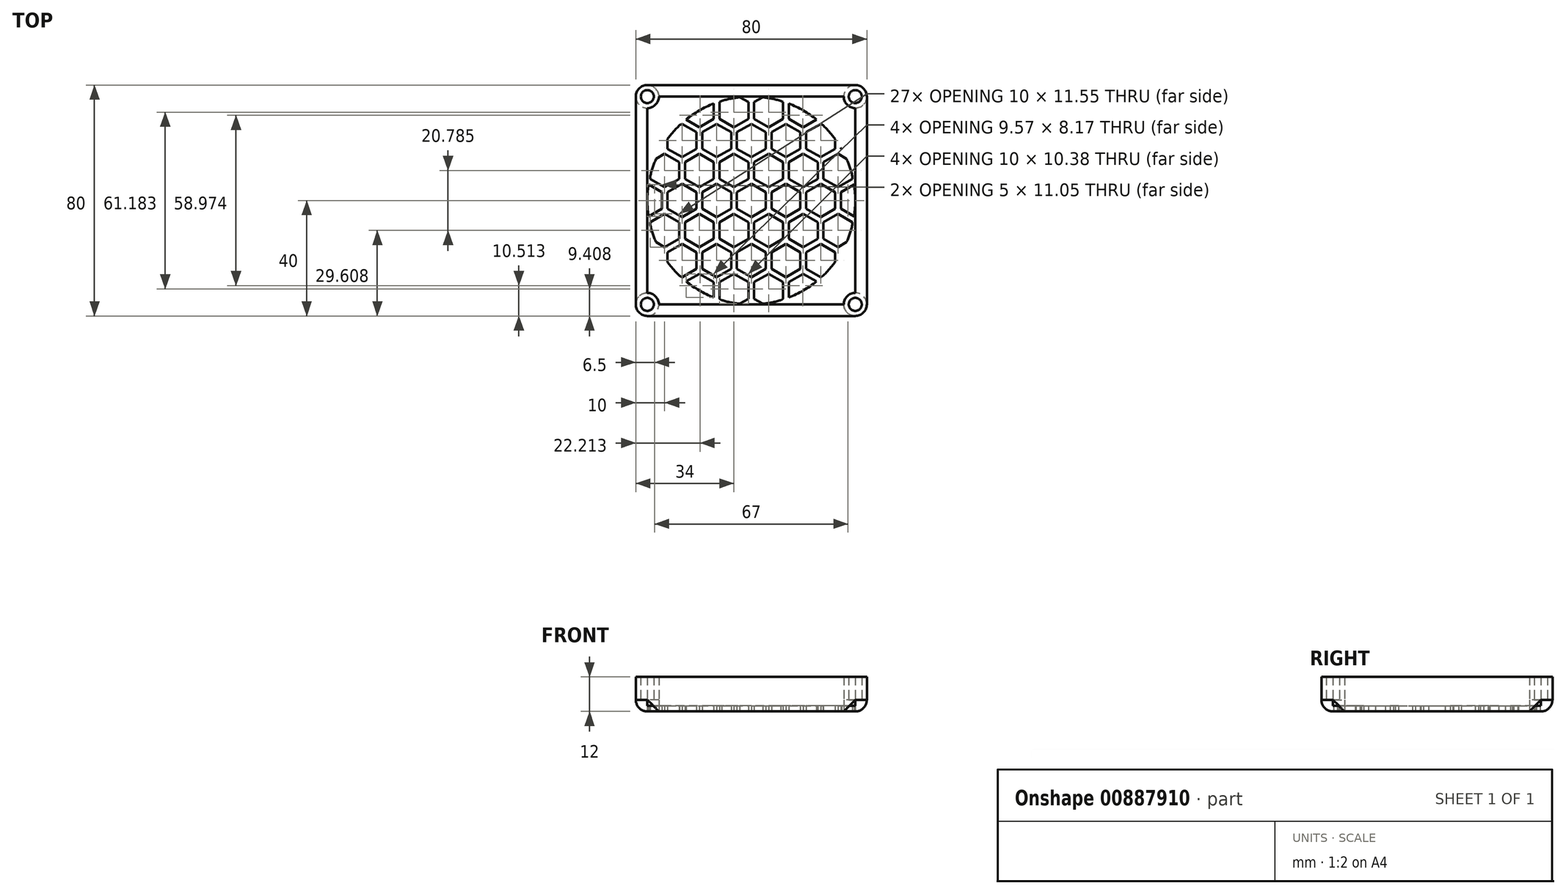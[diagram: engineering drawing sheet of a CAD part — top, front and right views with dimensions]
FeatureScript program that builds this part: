
annotation { "Feature Type Name" : "Feature", "Feature Type Description" : "" }
export const myFeature = defineFeature(function(context is Context, id is Id, definition is map)
    precondition{}
    {
        {
            var Q0;
            Q0=qCreatedBy(makeId("Top.planeOp"),FACE);
            var sketch = newSketch(context, id + "F0", { "sketchPlane" : qUnion([Q0])});
            skLineSegment(sketch, "E0.bottom", {"start": v(-36, 36) * mm, "end": v(36, 36) * mm});
            skLineSegment(sketch, "E0.top", {"start": v(-36, -36) * mm, "end": v(36, -36) * mm});
            skLineSegment(sketch, "E0.left", {"start": v(-36, 36) * mm, "end": v(-36, -36) * mm});
            skLineSegment(sketch, "E0.right", {"start": v(36, 36) * mm, "end": v(36, -36) * mm});
            skPoint(sketch, "E0.middle", {"position": v(0, 0) * mm});
            skCircle(sketch, "E1", {"center": v(-36, 36) * mm, "radius": 2.25 * mm});
            skCircle(sketch, "E2", {"center": v(36, 36) * mm, "radius": 2.25 * mm});
            skCircle(sketch, "E3", {"center": v(36, -36) * mm, "radius": 2.25 * mm});
            skCircle(sketch, "E4", {"center": v(-36, -36) * mm, "radius": 2.25 * mm});
            skLineSegment(sketch, "E5.bottom", {"start": v(-40, 40) * mm, "end": v(40, 40) * mm});
            skLineSegment(sketch, "E5.top", {"start": v(-40, -40) * mm, "end": v(40, -40) * mm});
            skLineSegment(sketch, "E5.left", {"start": v(-40, 40) * mm, "end": v(-40, -40) * mm});
            skLineSegment(sketch, "E5.right", {"start": v(40, 40) * mm, "end": v(40, -40) * mm});
            skCircle(sketch, "E6", {"center": v(0, 0) * mm, "radius": 36 * mm});
            skCircle(sketch, "E7.cCircle", {"center": v(0, 0) * mm, "radius": 5 * mm, "construction": true});
            skLineSegment(sketch, "E7.0", {"start": v(-5, -2.89) * mm, "end": v(-5, 2.89) * mm});
            skLineSegment(sketch, "E7.1", {"start": v(-5, 2.89) * mm, "end": v(0, 5.77) * mm});
            skLineSegment(sketch, "E7.2", {"start": v(0, 5.77) * mm, "end": v(5, 2.89) * mm});
            skLineSegment(sketch, "E7.3", {"start": v(5, 2.89) * mm, "end": v(5, -2.89) * mm});
            skLineSegment(sketch, "E7.4", {"start": v(5, -2.89) * mm, "end": v(0, -5.77) * mm});
            skLineSegment(sketch, "E7.5", {"start": v(0, -5.77) * mm, "end": v(-5, -2.89) * mm});
            skPoint(sketch, "E7.0.midPoint", {"position": v(-5, 0) * mm});
            skPoint(sketch, "E8.0.1.0", {"position": v(-5, 20.78) * mm});
            skLineSegment(sketch, "E8.0.1.1", {"start": v(5, 17.9) * mm, "end": v(0, 15.01) * mm});
            skPoint(sketch, "E8.0.1.3", {"position": v(0, 20.78) * mm});
            skLineSegment(sketch, "E8.0.1.4", {"start": v(0, 26.56) * mm, "end": v(5, 23.67) * mm});
            skLineSegment(sketch, "E8.0.1.5", {"start": v(0, 15.01) * mm, "end": v(-5, 17.9) * mm});
            skLineSegment(sketch, "E8.0.1.6", {"start": v(-5, 17.9) * mm, "end": v(-5, 23.67) * mm});
            skLineSegment(sketch, "E8.0.1.7", {"start": v(-5, 23.67) * mm, "end": v(0, 26.56) * mm});
            skLineSegment(sketch, "E8.0.1.8", {"start": v(5, 23.67) * mm, "end": v(5, 17.9) * mm});
            skPoint(sketch, "E8.0.1.9", {"position": v(0, 20.78) * mm});
            skPoint(sketch, "E8.0.1.10", {"position": v(0, 20.78) * mm});
            skPoint(sketch, "E8.0.1.11", {"position": v(0, 20.78) * mm});
            skPoint(sketch, "E8.1.0.0", {"position": v(7, 0) * mm});
            skLineSegment(sketch, "E8.1.0.1", {"start": v(17, -2.89) * mm, "end": v(12, -5.77) * mm});
            skCircle(sketch, "E8.1.0.2", {"center": v(12, 0) * mm, "radius": 5 * mm, "construction": true});
            skPoint(sketch, "E8.1.0.3", {"position": v(12, 0) * mm});
            skLineSegment(sketch, "E8.1.0.4", {"start": v(12, 5.77) * mm, "end": v(17, 2.89) * mm});
            skLineSegment(sketch, "E8.1.0.5", {"start": v(12, -5.77) * mm, "end": v(7, -2.89) * mm});
            skLineSegment(sketch, "E8.1.0.6", {"start": v(7, -2.89) * mm, "end": v(7, 2.89) * mm});
            skLineSegment(sketch, "E8.1.0.7", {"start": v(7, 2.89) * mm, "end": v(12, 5.77) * mm});
            skLineSegment(sketch, "E8.1.0.8", {"start": v(17, 2.89) * mm, "end": v(17, -2.89) * mm});
            skPoint(sketch, "E8.1.0.9", {"position": v(12, 0) * mm});
            skPoint(sketch, "E8.1.0.10", {"position": v(12, 0) * mm});
            skPoint(sketch, "E8.1.0.11", {"position": v(12, 0) * mm});
            skPoint(sketch, "E8.1.1.0", {"position": v(7, 20.78) * mm});
            skLineSegment(sketch, "E8.1.1.1", {"start": v(17, 17.9) * mm, "end": v(12, 15.01) * mm});
            skPoint(sketch, "E8.1.1.3", {"position": v(12, 20.78) * mm});
            skLineSegment(sketch, "E8.1.1.4", {"start": v(12, 26.56) * mm, "end": v(17, 23.67) * mm});
            skLineSegment(sketch, "E8.1.1.5", {"start": v(12, 15.01) * mm, "end": v(7, 17.9) * mm});
            skLineSegment(sketch, "E8.1.1.6", {"start": v(7, 17.9) * mm, "end": v(7, 23.67) * mm});
            skLineSegment(sketch, "E8.1.1.7", {"start": v(7, 23.67) * mm, "end": v(12, 26.56) * mm});
            skLineSegment(sketch, "E8.1.1.8", {"start": v(17, 23.67) * mm, "end": v(17, 17.9) * mm});
            skPoint(sketch, "E8.1.1.9", {"position": v(12, 20.78) * mm});
            skPoint(sketch, "E8.1.1.10", {"position": v(12, 20.78) * mm});
            skPoint(sketch, "E8.1.1.11", {"position": v(12, 20.78) * mm});
            skPoint(sketch, "E8.2.0.0", {"position": v(19, 0) * mm});
            skLineSegment(sketch, "E8.2.0.1", {"start": v(29, -2.89) * mm, "end": v(24, -5.77) * mm});
            skPoint(sketch, "E8.2.0.3", {"position": v(24, 0) * mm});
            skLineSegment(sketch, "E8.2.0.4", {"start": v(24, 5.77) * mm, "end": v(29, 2.89) * mm});
            skLineSegment(sketch, "E8.2.0.5", {"start": v(24, -5.77) * mm, "end": v(19, -2.89) * mm});
            skLineSegment(sketch, "E8.2.0.6", {"start": v(19, -2.89) * mm, "end": v(19, 2.89) * mm});
            skLineSegment(sketch, "E8.2.0.7", {"start": v(19, 2.89) * mm, "end": v(24, 5.77) * mm});
            skLineSegment(sketch, "E8.2.0.8", {"start": v(29, 2.89) * mm, "end": v(29, -2.89) * mm});
            skPoint(sketch, "E8.2.0.9", {"position": v(24, 0) * mm});
            skPoint(sketch, "E8.2.0.10", {"position": v(24, 0) * mm});
            skPoint(sketch, "E8.2.0.11", {"position": v(24, 0) * mm});
            skPoint(sketch, "E8.2.1.0", {"position": v(19, 20.78) * mm});
            skLineSegment(sketch, "E8.2.1.1", {"start": v(29, 17.9) * mm, "end": v(24, 15.01) * mm});
            skPoint(sketch, "E8.2.1.3", {"position": v(24, 20.78) * mm});
            skLineSegment(sketch, "E8.2.1.4", {"start": v(24, 26.56) * mm, "end": v(24.8, 26.1) * mm});
            skLineSegment(sketch, "E8.2.1.5", {"start": v(24, 15.01) * mm, "end": v(19, 17.9) * mm});
            skLineSegment(sketch, "E8.2.1.6", {"start": v(19, 17.9) * mm, "end": v(19, 23.67) * mm});
            skLineSegment(sketch, "E8.2.1.7", {"start": v(19, 23.67) * mm, "end": v(24, 26.56) * mm});
            skLineSegment(sketch, "E8.2.1.8", {"start": v(29, 21.33) * mm, "end": v(29, 17.9) * mm});
            skPoint(sketch, "E8.2.1.9", {"position": v(24, 20.78) * mm});
            skPoint(sketch, "E8.2.1.10", {"position": v(24, 20.78) * mm});
            skPoint(sketch, "E8.2.1.11", {"position": v(24, 20.78) * mm});
            skPoint(sketch, "E8.3.0.0", {"position": v(31, 0) * mm});
            skPoint(sketch, "E8.3.0.3", {"position": v(36, 0) * mm});
            skLineSegment(sketch, "E8.3.0.5", {"start": v(35.57, -5.53) * mm, "end": v(31, -2.89) * mm});
            skLineSegment(sketch, "E8.3.0.6", {"start": v(31, -2.89) * mm, "end": v(31, 2.89) * mm});
            skLineSegment(sketch, "E8.3.0.7", {"start": v(31, 2.89) * mm, "end": v(35.57, 5.53) * mm});
            skPoint(sketch, "E8.3.0.9", {"position": v(36, 0) * mm});
            skPoint(sketch, "E8.3.0.10", {"position": v(36, 0) * mm});
            skPoint(sketch, "E8.3.0.11", {"position": v(36, 0) * mm});
            skLineSegment(sketch, "E8.3.1.6", {"start": v(31, 17.9) * mm, "end": v(31, 18.3) * mm});
            skLineSegment(sketch, "E8.direction1", {"start": v(-5, 0) * mm, "end": v(7, 0) * mm, "construction": true});
            skLineSegment(sketch, "E8.direction2", {"start": v(-5, 0) * mm, "end": v(-5, 20.78) * mm, "construction": true});
            skCircle(sketch, "E9.cCircle", {"center": v(6, 10.4) * mm, "radius": 5 * mm, "construction": true});
            skLineSegment(sketch, "E9.0", {"start": v(6, 16.17) * mm, "end": v(11, 13.28) * mm});
            skLineSegment(sketch, "E9.1", {"start": v(11, 13.28) * mm, "end": v(11, 7.5) * mm});
            skLineSegment(sketch, "E9.2", {"start": v(11, 7.5) * mm, "end": v(6, 4.62) * mm});
            skLineSegment(sketch, "E9.3", {"start": v(6, 4.62) * mm, "end": v(1, 7.5) * mm});
            skLineSegment(sketch, "E9.4", {"start": v(1, 7.5) * mm, "end": v(1, 13.28) * mm});
            skLineSegment(sketch, "E9.5", {"start": v(1, 13.28) * mm, "end": v(6, 16.17) * mm});
            skLineSegment(sketch, "E10", {"start": v(7, 20.78) * mm, "end": v(5, 20.78) * mm, "construction": true});
            skPoint(sketch, "E11", {"position": v(6, 20.78) * mm});
            skPoint(sketch, "E12", {"position": v(1, 10.4) * mm});
            skLineSegment(sketch, "E13.0.1.0", {"start": v(1, 28.3) * mm, "end": v(1, 34.06) * mm});
            skLineSegment(sketch, "E13.0.1.1", {"start": v(11, 28.3) * mm, "end": v(6, 25.4) * mm});
            skLineSegment(sketch, "E13.0.1.2", {"start": v(6, 25.4) * mm, "end": v(1, 28.3) * mm});
            skLineSegment(sketch, "E13.0.1.4", {"start": v(11, 34.06) * mm, "end": v(11, 28.3) * mm});
            skLineSegment(sketch, "E13.0.1.6", {"start": v(1, 34.06) * mm, "end": v(3.97, 35.78) * mm});
            skPoint(sketch, "E13.0.1.7", {"position": v(1, 31.18) * mm});
            skLineSegment(sketch, "E13.1.0.0", {"start": v(13, 7.5) * mm, "end": v(13, 13.28) * mm});
            skLineSegment(sketch, "E13.1.0.1", {"start": v(23, 7.5) * mm, "end": v(18, 4.62) * mm});
            skLineSegment(sketch, "E13.1.0.2", {"start": v(18, 4.62) * mm, "end": v(13, 7.5) * mm});
            skLineSegment(sketch, "E13.1.0.4", {"start": v(23, 13.28) * mm, "end": v(23, 7.5) * mm});
            skLineSegment(sketch, "E13.1.0.5", {"start": v(18, 16.17) * mm, "end": v(23, 13.28) * mm});
            skLineSegment(sketch, "E13.1.0.6", {"start": v(13, 13.28) * mm, "end": v(18, 16.17) * mm});
            skPoint(sketch, "E13.1.0.7", {"position": v(13, 10.4) * mm});
            skLineSegment(sketch, "E13.1.1.0", {"start": v(13, 28.3) * mm, "end": v(13, 33.57) * mm});
            skLineSegment(sketch, "E13.1.1.1", {"start": v(22.57, 28.04) * mm, "end": v(18, 25.4) * mm});
            skLineSegment(sketch, "E13.1.1.2", {"start": v(18, 25.4) * mm, "end": v(13, 28.3) * mm});
            skPoint(sketch, "E13.1.1.7", {"position": v(13, 31.18) * mm});
            skLineSegment(sketch, "E13.2.0.0", {"start": v(25, 7.5) * mm, "end": v(25, 13.28) * mm});
            skLineSegment(sketch, "E13.2.0.1", {"start": v(35, 7.5) * mm, "end": v(30, 4.62) * mm});
            skLineSegment(sketch, "E13.2.0.2", {"start": v(30, 4.62) * mm, "end": v(25, 7.5) * mm});
            skLineSegment(sketch, "E13.2.0.4", {"start": v(35, 8.43) * mm, "end": v(35, 7.5) * mm});
            skLineSegment(sketch, "E13.2.0.5", {"start": v(30, 16.17) * mm, "end": v(32.97, 14.45) * mm});
            skLineSegment(sketch, "E13.2.0.6", {"start": v(25, 13.28) * mm, "end": v(30, 16.17) * mm});
            skPoint(sketch, "E13.2.0.7", {"position": v(25, 10.4) * mm});
            skLineSegment(sketch, "E13.direction1", {"start": v(1, 10.4) * mm, "end": v(13, 10.4) * mm, "construction": true});
            skLineSegment(sketch, "E13.direction2", {"start": v(1, 10.4) * mm, "end": v(1, 31.18) * mm, "construction": true});
            skLineSegment(sketch, "E14.trimOffspring", {"start": v(10.2, 34.52) * mm, "end": v(11, 34.06) * mm});
            skLineSegment(sketch, "E15.trimOffspring", {"start": v(31.35, 17.7) * mm, "end": v(31, 17.9) * mm});
            skLineSegment(sketch, "E16.MirrorCS", {"start": v(-6, 25.4) * mm, "end": v(-1, 28.3) * mm});
            skLineSegment(sketch, "E17.MirrorCS", {"start": v(-1, 28.3) * mm, "end": v(-1, 34.06) * mm});
            skLineSegment(sketch, "E18.MirrorCS", {"start": v(-1, 34.06) * mm, "end": v(-3.97, 35.78) * mm});
            skLineSegment(sketch, "E19.MirrorCS", {"start": v(-11, 34.06) * mm, "end": v(-11, 28.3) * mm});
            skLineSegment(sketch, "E20.MirrorCS", {"start": v(-10.2, 34.52) * mm, "end": v(-11, 34.06) * mm});
            skLineSegment(sketch, "E21.MirrorCS", {"start": v(-11, 28.3) * mm, "end": v(-6, 25.4) * mm});
            skLineSegment(sketch, "E22.MirrorCS", {"start": v(-18, 25.4) * mm, "end": v(-13, 28.3) * mm});
            skLineSegment(sketch, "E23.MirrorCS", {"start": v(-13, 28.3) * mm, "end": v(-13, 33.57) * mm});
            skLineSegment(sketch, "E24.MirrorCS", {"start": v(-22.57, 28.04) * mm, "end": v(-18, 25.4) * mm});
            skLineSegment(sketch, "E25.MirrorCS", {"start": v(-7, 23.67) * mm, "end": v(-12, 26.56) * mm});
            skLineSegment(sketch, "E26.MirrorCS", {"start": v(-12, 26.56) * mm, "end": v(-17, 23.67) * mm});
            skLineSegment(sketch, "E27.MirrorCS", {"start": v(-17, 23.67) * mm, "end": v(-17, 17.9) * mm});
            skLineSegment(sketch, "E28.MirrorCS", {"start": v(-17, 17.9) * mm, "end": v(-12, 15.01) * mm});
            skLineSegment(sketch, "E29.MirrorCS", {"start": v(-12, 15.01) * mm, "end": v(-7, 17.9) * mm});
            skLineSegment(sketch, "E30.MirrorCS", {"start": v(-7, 17.9) * mm, "end": v(-7, 23.67) * mm});
            skLineSegment(sketch, "E31.MirrorCS", {"start": v(-1, 13.28) * mm, "end": v(-6, 16.17) * mm});
            skLineSegment(sketch, "E32.MirrorCS", {"start": v(-6, 16.17) * mm, "end": v(-11, 13.28) * mm});
            skLineSegment(sketch, "E33.MirrorCS", {"start": v(-11, 13.28) * mm, "end": v(-11, 7.5) * mm});
            skLineSegment(sketch, "E34.MirrorCS", {"start": v(-11, 7.5) * mm, "end": v(-6, 4.62) * mm});
            skLineSegment(sketch, "E35.MirrorCS", {"start": v(-6, 4.62) * mm, "end": v(-1, 7.5) * mm});
            skLineSegment(sketch, "E36.MirrorCS", {"start": v(-1, 7.5) * mm, "end": v(-1, 13.28) * mm});
            skLineSegment(sketch, "E37.MirrorCS", {"start": v(-12, -5.77) * mm, "end": v(-7, -2.89) * mm});
            skLineSegment(sketch, "E38.MirrorCS", {"start": v(-7, -2.89) * mm, "end": v(-7, 2.89) * mm});
            skLineSegment(sketch, "E39.MirrorCS", {"start": v(-7, 2.89) * mm, "end": v(-12, 5.77) * mm});
            skLineSegment(sketch, "E40.MirrorCS", {"start": v(-12, 5.77) * mm, "end": v(-17, 2.89) * mm});
            skLineSegment(sketch, "E41.MirrorCS", {"start": v(-17, 2.89) * mm, "end": v(-17, -2.89) * mm});
            skLineSegment(sketch, "E42.MirrorCS", {"start": v(-17, -2.89) * mm, "end": v(-12, -5.77) * mm});
            skLineSegment(sketch, "E43.MirrorCS", {"start": v(-24, -5.77) * mm, "end": v(-19, -2.89) * mm});
            skLineSegment(sketch, "E44.MirrorCS", {"start": v(-29, -2.89) * mm, "end": v(-24, -5.77) * mm});
            skLineSegment(sketch, "E45.MirrorCS", {"start": v(-29, 2.89) * mm, "end": v(-29, -2.89) * mm});
            skLineSegment(sketch, "E46.MirrorCS", {"start": v(-24, 5.77) * mm, "end": v(-29, 2.89) * mm});
            skLineSegment(sketch, "E47.MirrorCS", {"start": v(-19, 2.89) * mm, "end": v(-24, 5.77) * mm});
            skLineSegment(sketch, "E48.MirrorCS", {"start": v(-19, -2.89) * mm, "end": v(-19, 2.89) * mm});
            skLineSegment(sketch, "E49.MirrorCS", {"start": v(-35.57, -5.53) * mm, "end": v(-31, -2.89) * mm});
            skLineSegment(sketch, "E50.MirrorCS", {"start": v(-31, -2.89) * mm, "end": v(-31, 2.89) * mm});
            skLineSegment(sketch, "E51.MirrorCS", {"start": v(-31, 2.89) * mm, "end": v(-35.57, 5.53) * mm});
            skLineSegment(sketch, "E52.MirrorCS", {"start": v(-35, 7.5) * mm, "end": v(-30, 4.62) * mm});
            skLineSegment(sketch, "E53.MirrorCS", {"start": v(-30, 4.62) * mm, "end": v(-25, 7.5) * mm});
            skLineSegment(sketch, "E54.MirrorCS", {"start": v(-25, 7.5) * mm, "end": v(-25, 13.28) * mm});
            skLineSegment(sketch, "E55.MirrorCS", {"start": v(-25, 13.28) * mm, "end": v(-30, 16.17) * mm});
            skLineSegment(sketch, "E56.MirrorCS", {"start": v(-30, 16.17) * mm, "end": v(-32.97, 14.45) * mm});
            skLineSegment(sketch, "E57.MirrorCS", {"start": v(-23, 7.5) * mm, "end": v(-18, 4.62) * mm});
            skLineSegment(sketch, "E58.MirrorCS", {"start": v(-23, 13.28) * mm, "end": v(-23, 7.5) * mm});
            skLineSegment(sketch, "E59.MirrorCS", {"start": v(-18, 16.17) * mm, "end": v(-23, 13.28) * mm});
            skLineSegment(sketch, "E60.MirrorCS", {"start": v(-13, 13.28) * mm, "end": v(-18, 16.17) * mm});
            skLineSegment(sketch, "E61.MirrorCS", {"start": v(-13, 7.5) * mm, "end": v(-13, 13.28) * mm});
            skLineSegment(sketch, "E62.MirrorCS", {"start": v(-18, 4.62) * mm, "end": v(-13, 7.5) * mm});
            skLineSegment(sketch, "E63.MirrorCS", {"start": v(-29, 17.9) * mm, "end": v(-24, 15.01) * mm});
            skLineSegment(sketch, "E64.MirrorCS", {"start": v(-24, 15.01) * mm, "end": v(-19, 17.9) * mm});
            skLineSegment(sketch, "E65.MirrorCS", {"start": v(-19, 17.9) * mm, "end": v(-19, 23.67) * mm});
            skLineSegment(sketch, "E66.MirrorCS", {"start": v(-19, 23.67) * mm, "end": v(-24, 26.56) * mm});
            skLineSegment(sketch, "E67.MirrorCS", {"start": v(-24, 26.56) * mm, "end": v(-24.8, 26.1) * mm});
            skLineSegment(sketch, "E68.MirrorCS", {"start": v(-29, 21.33) * mm, "end": v(-29, 17.9) * mm});
            skLineSegment(sketch, "E69.MirrorCS", {"start": v(-19, -17.9) * mm, "end": v(-19, -23.67) * mm});
            skLineSegment(sketch, "E70.MirrorCS", {"start": v(-17, -23.67) * mm, "end": v(-17, -17.9) * mm});
            skLineSegment(sketch, "E71.MirrorCS", {"start": v(-30, -16.17) * mm, "end": v(-32.97, -14.45) * mm});
            skLineSegment(sketch, "E72.MirrorCS", {"start": v(-29, -21.33) * mm, "end": v(-29, -17.9) * mm});
            skLineSegment(sketch, "E73.MirrorCS", {"start": v(-35, -7.5) * mm, "end": v(-30, -4.62) * mm});
            skLineSegment(sketch, "E74.MirrorCS", {"start": v(-23, -13.28) * mm, "end": v(-23, -7.5) * mm});
            skLineSegment(sketch, "E75.MirrorCS", {"start": v(-31, 2.89) * mm, "end": v(-31, -2.89) * mm});
            skLineSegment(sketch, "E76.MirrorCS", {"start": v(-30, -4.62) * mm, "end": v(-25, -7.5) * mm});
            skLineSegment(sketch, "E77.MirrorCS", {"start": v(-24, 5.77) * mm, "end": v(-19, 2.89) * mm});
            skLineSegment(sketch, "E78.MirrorCS", {"start": v(-7, -2.89) * mm, "end": v(-12, -5.77) * mm});
            skLineSegment(sketch, "E79.MirrorCS", {"start": v(-19, 2.89) * mm, "end": v(-19, -2.89) * mm});
            skLineSegment(sketch, "E80.MirrorCS", {"start": v(-11, -7.5) * mm, "end": v(-6, -4.62) * mm});
            skLineSegment(sketch, "E81.MirrorCS", {"start": v(-29, -2.89) * mm, "end": v(-29, 2.89) * mm});
            skLineSegment(sketch, "E82.MirrorCS", {"start": v(-18, -4.62) * mm, "end": v(-13, -7.5) * mm});
            skLineSegment(sketch, "E83.MirrorCS", {"start": v(-12, -5.77) * mm, "end": v(-17, -2.89) * mm});
            skLineSegment(sketch, "E84.MirrorCS", {"start": v(-29, -17.9) * mm, "end": v(-24, -15.01) * mm});
            skLineSegment(sketch, "E85.MirrorCS", {"start": v(-18, -16.17) * mm, "end": v(-23, -13.28) * mm});
            skLineSegment(sketch, "E86.MirrorCS", {"start": v(-6, -16.17) * mm, "end": v(-11, -13.28) * mm});
            skLineSegment(sketch, "E87.MirrorCS", {"start": v(-25, -7.5) * mm, "end": v(-25, -13.28) * mm});
            skLineSegment(sketch, "E88.MirrorCS", {"start": v(-11, -13.28) * mm, "end": v(-11, -7.5) * mm});
            skLineSegment(sketch, "E89.MirrorCS", {"start": v(-17, 2.89) * mm, "end": v(-12, 5.77) * mm});
            skLineSegment(sketch, "E90.MirrorCS", {"start": v(-12, 5.77) * mm, "end": v(-7, 2.89) * mm});
            skLineSegment(sketch, "E91.MirrorCS", {"start": v(-23, -7.5) * mm, "end": v(-18, -4.62) * mm});
            skLineSegment(sketch, "E92.MirrorCS", {"start": v(-17, -17.9) * mm, "end": v(-12, -15.01) * mm});
            skLineSegment(sketch, "E93.MirrorCS", {"start": v(-29, 2.89) * mm, "end": v(-24, 5.77) * mm});
            skLineSegment(sketch, "E94.MirrorCS", {"start": v(-13, -13.28) * mm, "end": v(-18, -16.17) * mm});
            skLineSegment(sketch, "E95.MirrorCS", {"start": v(-17, -2.89) * mm, "end": v(-17, 2.89) * mm});
            skLineSegment(sketch, "E96.MirrorCS", {"start": v(-24, -5.77) * mm, "end": v(-29, -2.89) * mm});
            skLineSegment(sketch, "E97.MirrorCS", {"start": v(-13, -7.5) * mm, "end": v(-13, -13.28) * mm});
            skLineSegment(sketch, "E98.MirrorCS", {"start": v(-24, -15.01) * mm, "end": v(-19, -17.9) * mm});
            skLineSegment(sketch, "E99.MirrorCS", {"start": v(-25, -13.28) * mm, "end": v(-30, -16.17) * mm});
            skLineSegment(sketch, "E100.MirrorCS", {"start": v(-19, -2.89) * mm, "end": v(-24, -5.77) * mm});
            skLineSegment(sketch, "E101.MirrorCS", {"start": v(-12, -15.01) * mm, "end": v(-7, -17.9) * mm});
            skLineSegment(sketch, "E102.MirrorCS", {"start": v(-24, -26.56) * mm, "end": v(-24.8, -26.1) * mm});
            skLineSegment(sketch, "E103.MirrorCS", {"start": v(-35, 8.43) * mm, "end": v(-35, 7.5) * mm});
            skLineSegment(sketch, "E104.MirrorCS", {"start": v(-35, -8.43) * mm, "end": v(-35, -7.5) * mm});
            skLineSegment(sketch, "E105.MirrorCS", {"start": v(-19, -23.67) * mm, "end": v(-24, -26.56) * mm});
            skLineSegment(sketch, "E106.MirrorCS", {"start": v(-6, -4.62) * mm, "end": v(-1, -7.5) * mm});
            skLineSegment(sketch, "E107.MirrorCS", {"start": v(-1, -7.5) * mm, "end": v(-1, -13.28) * mm});
            skLineSegment(sketch, "E108.MirrorCS", {"start": v(-5, -23.67) * mm, "end": v(0, -26.56) * mm});
            skLineSegment(sketch, "E109.MirrorCS", {"start": v(0, -26.56) * mm, "end": v(5, -23.67) * mm});
            skLineSegment(sketch, "E110.MirrorCS", {"start": v(5, -23.67) * mm, "end": v(5, -17.9) * mm});
            skLineSegment(sketch, "E111.MirrorCS", {"start": v(5, -17.9) * mm, "end": v(0, -15.01) * mm});
            skLineSegment(sketch, "E112.MirrorCS", {"start": v(0, -15.01) * mm, "end": v(-5, -17.9) * mm});
            skLineSegment(sketch, "E113.MirrorCS", {"start": v(-5, -17.9) * mm, "end": v(-5, -23.67) * mm});
            skLineSegment(sketch, "E114.MirrorCS", {"start": v(-1, -13.28) * mm, "end": v(-6, -16.17) * mm});
            skLineSegment(sketch, "E115.MirrorCS", {"start": v(-6, -25.4) * mm, "end": v(-1, -28.3) * mm});
            skLineSegment(sketch, "E116.MirrorCS", {"start": v(-1, -28.3) * mm, "end": v(-1, -34.06) * mm});
            skLineSegment(sketch, "E117.MirrorCS", {"start": v(-11, -28.3) * mm, "end": v(-6, -25.4) * mm});
            skLineSegment(sketch, "E118.MirrorCS", {"start": v(-11, -34.06) * mm, "end": v(-11, -28.3) * mm});
            skLineSegment(sketch, "E119.MirrorCS", {"start": v(-10.2, -34.52) * mm, "end": v(-11, -34.06) * mm});
            skLineSegment(sketch, "E120.MirrorCS", {"start": v(-18, -25.4) * mm, "end": v(-13, -28.3) * mm});
            skLineSegment(sketch, "E121.MirrorCS", {"start": v(-13, -28.3) * mm, "end": v(-13, -33.57) * mm});
            skLineSegment(sketch, "E122.MirrorCS", {"start": v(-22.57, -28.04) * mm, "end": v(-18, -25.4) * mm});
            skLineSegment(sketch, "E123.MirrorCS", {"start": v(-12, -26.56) * mm, "end": v(-17, -23.67) * mm});
            skLineSegment(sketch, "E124.MirrorCS", {"start": v(-7, -23.67) * mm, "end": v(-12, -26.56) * mm});
            skLineSegment(sketch, "E125.MirrorCS", {"start": v(-7, -17.9) * mm, "end": v(-7, -23.67) * mm});
            skLineSegment(sketch, "E126.MirrorCS", {"start": v(-1, -34.06) * mm, "end": v(-3.97, -35.78) * mm});
            skLineSegment(sketch, "E127.MirrorCS", {"start": v(6, -4.62) * mm, "end": v(1, -7.5) * mm});
            skLineSegment(sketch, "E128.MirrorCS", {"start": v(11, -7.5) * mm, "end": v(6, -4.62) * mm});
            skLineSegment(sketch, "E129.MirrorCS", {"start": v(11, -13.28) * mm, "end": v(11, -7.5) * mm});
            skLineSegment(sketch, "E130.MirrorCS", {"start": v(6, -16.17) * mm, "end": v(11, -13.28) * mm});
            skLineSegment(sketch, "E131.MirrorCS", {"start": v(1, -13.28) * mm, "end": v(6, -16.17) * mm});
            skLineSegment(sketch, "E132.MirrorCS", {"start": v(1, -7.5) * mm, "end": v(1, -13.28) * mm});
            skLineSegment(sketch, "E133.MirrorCS", {"start": v(23, -7.5) * mm, "end": v(18, -4.62) * mm});
            skLineSegment(sketch, "E134.MirrorCS", {"start": v(18, -4.62) * mm, "end": v(13, -7.5) * mm});
            skLineSegment(sketch, "E135.MirrorCS", {"start": v(13, -7.5) * mm, "end": v(13, -13.28) * mm});
            skLineSegment(sketch, "E136.MirrorCS", {"start": v(13, -13.28) * mm, "end": v(18, -16.17) * mm});
            skLineSegment(sketch, "E137.MirrorCS", {"start": v(18, -16.17) * mm, "end": v(23, -13.28) * mm});
            skLineSegment(sketch, "E138.MirrorCS", {"start": v(23, -13.28) * mm, "end": v(23, -7.5) * mm});
            skLineSegment(sketch, "E139.MirrorCS", {"start": v(30, -4.62) * mm, "end": v(25, -7.5) * mm});
            skLineSegment(sketch, "E140.MirrorCS", {"start": v(25, -7.5) * mm, "end": v(25, -13.28) * mm});
            skLineSegment(sketch, "E141.MirrorCS", {"start": v(25, -13.28) * mm, "end": v(30, -16.17) * mm});
            skLineSegment(sketch, "E142.MirrorCS", {"start": v(30, -16.17) * mm, "end": v(32.97, -14.45) * mm});
            skLineSegment(sketch, "E143.MirrorCS", {"start": v(35, -7.5) * mm, "end": v(30, -4.62) * mm});
            skLineSegment(sketch, "E144.MirrorCS", {"start": v(35, -8.43) * mm, "end": v(35, -7.5) * mm});
            skLineSegment(sketch, "E145.MirrorCS", {"start": v(12, -15.01) * mm, "end": v(7, -17.9) * mm});
            skLineSegment(sketch, "E146.MirrorCS", {"start": v(17, -17.9) * mm, "end": v(12, -15.01) * mm});
            skLineSegment(sketch, "E147.MirrorCS", {"start": v(17, -23.67) * mm, "end": v(17, -17.9) * mm});
            skLineSegment(sketch, "E148.MirrorCS", {"start": v(12, -26.56) * mm, "end": v(17, -23.67) * mm});
            skLineSegment(sketch, "E149.MirrorCS", {"start": v(7, -23.67) * mm, "end": v(12, -26.56) * mm});
            skLineSegment(sketch, "E150.MirrorCS", {"start": v(7, -17.9) * mm, "end": v(7, -23.67) * mm});
            skLineSegment(sketch, "E151.MirrorCS", {"start": v(24, -15.01) * mm, "end": v(19, -17.9) * mm});
            skLineSegment(sketch, "E152.MirrorCS", {"start": v(29, -17.9) * mm, "end": v(24, -15.01) * mm});
            skLineSegment(sketch, "E153.MirrorCS", {"start": v(29, -21.33) * mm, "end": v(29, -17.9) * mm});
            skLineSegment(sketch, "E154.MirrorCS", {"start": v(19, -17.9) * mm, "end": v(19, -23.67) * mm});
            skLineSegment(sketch, "E155.MirrorCS", {"start": v(19, -23.67) * mm, "end": v(24, -26.56) * mm});
            skLineSegment(sketch, "E156.MirrorCS", {"start": v(24, -26.56) * mm, "end": v(24.8, -26.1) * mm});
            skLineSegment(sketch, "E157.MirrorCS", {"start": v(11, -28.3) * mm, "end": v(6, -25.4) * mm});
            skLineSegment(sketch, "E158.MirrorCS", {"start": v(6, -25.4) * mm, "end": v(1, -28.3) * mm});
            skLineSegment(sketch, "E159.MirrorCS", {"start": v(1, -28.3) * mm, "end": v(1, -34.06) * mm});
            skLineSegment(sketch, "E160.MirrorCS", {"start": v(1, -34.06) * mm, "end": v(3.97, -35.78) * mm});
            skLineSegment(sketch, "E161.MirrorCS", {"start": v(11, -34.06) * mm, "end": v(11, -28.3) * mm});
            skLineSegment(sketch, "E162.MirrorCS", {"start": v(13, -28.3) * mm, "end": v(13, -33.57) * mm});
            skLineSegment(sketch, "E163.MirrorCS", {"start": v(18, -25.4) * mm, "end": v(13, -28.3) * mm});
            skLineSegment(sketch, "E164.MirrorCS", {"start": v(22.57, -28.04) * mm, "end": v(18, -25.4) * mm});
            skLineSegment(sketch, "E165.MirrorCS", {"start": v(10.2, -34.52) * mm, "end": v(11, -34.06) * mm});
            skCircle(sketch, "E166", {"center": v(-36, 36) * mm, "radius": 4 * mm});
            skCircle(sketch, "E167.MirrorC", {"center": v(36, 36) * mm, "radius": 4 * mm});
            skCircle(sketch, "E168.MirrorC", {"center": v(36, -36) * mm, "radius": 4 * mm});
            skCircle(sketch, "E169.MirrorC", {"center": v(-36, -36) * mm, "radius": 4 * mm});
            skSolve(sketch);
        }
        {
            var Q0;
            Q0=makeQuery(id+"F0.imprint","IMPRINT",FACE,{"disambiguationData":[TD([[makeQuery(id+"F0.imprint","IMPRINT",EDGE,{"derivedFrom":sQuery(id+"F0.wireOp",EDGE,"E1")}),-1.0]])]});
            var Q1;
            Q1=makeQuery(id+"F0.imprint","IMPRINT",FACE,{"disambiguationData":[TD([[makeQuery(id+"F0.imprint","IMPRINT",EDGE,{"derivedFrom":sQuery(id+"F0.wireOp",EDGE,"E7.0")}),1.0]])]});
            var Q2;
            {var subQ19=sQuery(id+"F0.wireOp",EDGE,"E166");var subQ20=sQuery(id+"F0.wireOp",EDGE,"E5.bottom");var subQ21=makeQuery(id+"F0.imprint","INTERSECT",VERTEX,{"derivedFrom":[subQ20,subQ19]});Q2=makeQuery(id+"F0.imprint","IMPRINT",FACE,{"disambiguationData":[TD([[makeQuery(id+"F0.imprint","IMPRINT",EDGE,{"disambiguationData":[TD([[subQ21,-1.0]])],"derivedFrom":subQ20}),-1.0]])]});}
            var Q3;
            {var subQ0=sQuery(id+"F0.wireOp",EDGE,"E5.left");var subQ1=sQuery(id+"F0.wireOp",EDGE,"E5.bottom");var subQ2=makeQuery(id+"F0.imprint","INTERSECT",VERTEX,{"derivedFrom":[subQ1,subQ0]});Q3=makeQuery(id+"F0.imprint","IMPRINT",FACE,{"disambiguationData":[TD([[makeQuery(id+"F0.imprint","IMPRINT",EDGE,{"disambiguationData":[TD([[subQ2,-1.0]])],"derivedFrom":subQ1}),-1.0]])]});}
            var Q4;
            {var subQ0=sQuery(id+"F0.wireOp",EDGE,"E5.left");var subQ1=sQuery(id+"F0.wireOp",EDGE,"E5.top");var subQ2=makeQuery(id+"F0.imprint","INTERSECT",VERTEX,{"derivedFrom":[subQ1,subQ0]});Q4=makeQuery(id+"F0.imprint","IMPRINT",FACE,{"disambiguationData":[TD([[makeQuery(id+"F0.imprint","IMPRINT",EDGE,{"disambiguationData":[TD([[subQ2,-1.0]])],"derivedFrom":subQ1}),1.0]])]});}
            var Q5;
            Q5=makeQuery(id+"F0.imprint","IMPRINT",FACE,{"disambiguationData":[TD([[makeQuery(id+"F0.imprint","IMPRINT",EDGE,{"derivedFrom":sQuery(id+"F0.wireOp",EDGE,"E4")}),-1.0]])]});
            var Q6;
            {var subQ0=sQuery(id+"F0.wireOp",EDGE,"E5.right");var subQ1=sQuery(id+"F0.wireOp",EDGE,"E5.top");var subQ2=makeQuery(id+"F0.imprint","INTERSECT",VERTEX,{"derivedFrom":[subQ1,subQ0]});Q6=makeQuery(id+"F0.imprint","IMPRINT",FACE,{"disambiguationData":[TD([[makeQuery(id+"F0.imprint","IMPRINT",EDGE,{"disambiguationData":[TD([[subQ2,1.0]])],"derivedFrom":subQ1}),1.0]])]});}
            var Q7;
            Q7=makeQuery(id+"F0.imprint","IMPRINT",FACE,{"disambiguationData":[TD([[makeQuery(id+"F0.imprint","IMPRINT",EDGE,{"derivedFrom":sQuery(id+"F0.wireOp",EDGE,"E3")}),-1.0]])]});
            var Q8;
            {var subQ0=sQuery(id+"F0.wireOp",EDGE,"E5.right");var subQ1=sQuery(id+"F0.wireOp",EDGE,"E5.bottom");var subQ2=makeQuery(id+"F0.imprint","INTERSECT",VERTEX,{"derivedFrom":[subQ1,subQ0]});Q8=makeQuery(id+"F0.imprint","IMPRINT",FACE,{"disambiguationData":[TD([[makeQuery(id+"F0.imprint","IMPRINT",EDGE,{"disambiguationData":[TD([[subQ2,1.0]])],"derivedFrom":subQ1}),-1.0]])]});}
            var Q9;
            Q9=makeQuery(id+"F0.imprint","IMPRINT",FACE,{"disambiguationData":[TD([[makeQuery(id+"F0.imprint","IMPRINT",EDGE,{"derivedFrom":sQuery(id+"F0.wireOp",EDGE,"E2")}),-1.0]])]});
            var Q10;
            {var subQ6=sQuery(id+"F0.wireOp",EDGE,"E166");var subQ11=sQuery(id+"F0.wireOp",EDGE,"E0.bottom");var subQ12=makeQuery(id+"F0.imprint","INTERSECT",VERTEX,{"derivedFrom":[subQ11,subQ6]});Q10=makeQuery(id+"F0.imprint","IMPRINT",FACE,{"disambiguationData":[TD([[makeQuery(id+"F0.imprint","IMPRINT",EDGE,{"disambiguationData":[TD([[subQ12,-1.0]])],"derivedFrom":subQ11}),-1.0]])]});}
            var Q11;
            {var subQ0=sQuery(id+"F0.wireOp",EDGE,"E0.left");var subQ4=sQuery(id+"F0.wireOp",EDGE,"E166");var subQ7=makeQuery(id+"F0.imprint","INTERSECT",VERTEX,{"derivedFrom":[subQ0,subQ4]});Q11=makeQuery(id+"F0.imprint","IMPRINT",FACE,{"disambiguationData":[TD([[makeQuery(id+"F0.imprint","IMPRINT",EDGE,{"disambiguationData":[TD([[subQ7,-1.0]])],"derivedFrom":subQ0}),-1.0]])]});}
            var Q12;
            {var subQ8=sQuery(id+"F0.wireOp",EDGE,"E169.MirrorC");var subQ9=sQuery(id+"F0.wireOp",EDGE,"E0.top");var subQ10=makeQuery(id+"F0.imprint","INTERSECT",VERTEX,{"derivedFrom":[subQ9,subQ8]});Q12=makeQuery(id+"F0.imprint","IMPRINT",FACE,{"disambiguationData":[TD([[makeQuery(id+"F0.imprint","IMPRINT",EDGE,{"disambiguationData":[TD([[subQ10,-1.0]])],"derivedFrom":subQ9}),1.0]])]});}
            var Q13;
            {var subQ0=sQuery(id+"F0.wireOp",EDGE,"E6");var subQ8=sQuery(id+"F0.wireOp",EDGE,"E0.top");var subQ9=makeQuery(id+"F0.imprint","INTERSECT",VERTEX,{"derivedFrom":[subQ8,subQ0]});Q13=makeQuery(id+"F0.imprint","IMPRINT",FACE,{"disambiguationData":[TD([[makeQuery(id+"F0.imprint","IMPRINT",EDGE,{"disambiguationData":[TD([[subQ9,-1.0]])],"derivedFrom":subQ8}),1.0]])]});}
            var Q14;
            {var subQ0=sQuery(id+"F0.wireOp",EDGE,"E6");var subQ5=sQuery(id+"F0.wireOp",EDGE,"E0.bottom");var subQ6=makeQuery(id+"F0.imprint","INTERSECT",VERTEX,{"derivedFrom":[subQ5,subQ0]});Q14=makeQuery(id+"F0.imprint","IMPRINT",FACE,{"disambiguationData":[TD([[makeQuery(id+"F0.imprint","IMPRINT",EDGE,{"disambiguationData":[TD([[subQ6,-1.0]])],"derivedFrom":subQ5}),-1.0]])]});}
            var Q15;
            {var subQ0=sQuery(id+"F0.wireOp",EDGE,"E167.MirrorC");var subQ3=sQuery(id+"F0.wireOp",EDGE,"E0.right");var subQ4=makeQuery(id+"F0.imprint","INTERSECT",VERTEX,{"derivedFrom":[subQ3,subQ0]});Q15=makeQuery(id+"F0.imprint","IMPRINT",FACE,{"disambiguationData":[TD([[makeQuery(id+"F0.imprint","IMPRINT",EDGE,{"disambiguationData":[TD([[subQ4,-1.0]])],"derivedFrom":subQ3}),1.0]])]});}
            var Q16;
            {var subQ3=sQuery(id+"F0.wireOp",EDGE,"E0.top");var subQ5=sQuery(id+"F0.wireOp",EDGE,"E169.MirrorC");var subQ8=makeQuery(id+"F0.imprint","INTERSECT",VERTEX,{"derivedFrom":[subQ3,subQ5]});Q16=makeQuery(id+"F0.imprint","IMPRINT",FACE,{"disambiguationData":[TD([[makeQuery(id+"F0.imprint","IMPRINT",EDGE,{"disambiguationData":[TD([[subQ8,-1.0]])],"derivedFrom":subQ3}),-1.0]])]});}
            var Q17;
            {var subQ2=sQuery(id+"F0.wireOp",EDGE,"E0.top");var subQ4=sQuery(id+"F0.wireOp",EDGE,"E4");var subQ5=makeQuery(id+"F0.imprint","INTERSECT",VERTEX,{"derivedFrom":[subQ2,subQ4]});Q17=makeQuery(id+"F0.imprint","IMPRINT",FACE,{"disambiguationData":[TD([[makeQuery(id+"F0.imprint","IMPRINT",EDGE,{"disambiguationData":[TD([[subQ5,-1.0]])],"derivedFrom":subQ2}),-1.0]])]});}
            var Q18;
            {var subQ1=sQuery(id+"F0.wireOp",EDGE,"E0.top");var subQ5=sQuery(id+"F0.wireOp",EDGE,"E168.MirrorC");var subQ8=makeQuery(id+"F0.imprint","INTERSECT",VERTEX,{"derivedFrom":[subQ1,subQ5]});Q18=makeQuery(id+"F0.imprint","IMPRINT",FACE,{"disambiguationData":[TD([[makeQuery(id+"F0.imprint","IMPRINT",EDGE,{"disambiguationData":[TD([[subQ8,-1.0]])],"derivedFrom":subQ1}),-1.0]])]});}
            var Q19;
            {var subQ0=sQuery(id+"F0.wireOp",EDGE,"E167.MirrorC");var subQ2=sQuery(id+"F0.wireOp",EDGE,"E0.bottom");var subQ3=makeQuery(id+"F0.imprint","INTERSECT",VERTEX,{"derivedFrom":[subQ2,subQ0]});Q19=makeQuery(id+"F0.imprint","IMPRINT",FACE,{"disambiguationData":[TD([[makeQuery(id+"F0.imprint","IMPRINT",EDGE,{"disambiguationData":[TD([[subQ3,-1.0]])],"derivedFrom":subQ2}),1.0]])]});}
            var Q20;
            {var subQ2=sQuery(id+"F0.wireOp",EDGE,"E0.bottom");var subQ4=sQuery(id+"F0.wireOp",EDGE,"E1");var subQ5=makeQuery(id+"F0.imprint","INTERSECT",VERTEX,{"derivedFrom":[subQ2,subQ4]});Q20=makeQuery(id+"F0.imprint","IMPRINT",FACE,{"disambiguationData":[TD([[makeQuery(id+"F0.imprint","IMPRINT",EDGE,{"disambiguationData":[TD([[subQ5,-1.0]])],"derivedFrom":subQ2}),1.0]])]});}
            extrude(context, id + "F1", {"entities" : qUnion([Q0, Q1, Q2, Q3, Q4, Q5, Q6, Q7, Q8, Q9, Q10, Q11, Q12, Q13, Q14, Q15, Q16, Q17, Q18, Q19, Q20]), "depth" : 2 * mm, "offsetDistance" : 25 * mm});
        }
        {
            var Q0;
            Q0=makeQuery(id+"F1.opExtrude","SWEPT_EDGE",EDGE,{"disambiguationData":[OSD([sQuery(id+"F0.wireOp",EDGE,"E5.bottom"),sQuery(id+"F0.wireOp",EDGE,"E5.left")])]});
            var Q1;
            Q1=makeQuery(id+"F1.opExtrude","SWEPT_EDGE",EDGE,{"disambiguationData":[OSD([sQuery(id+"F0.wireOp",EDGE,"E5.bottom"),sQuery(id+"F0.wireOp",EDGE,"E5.right")])]});
            var Q2;
            Q2=makeQuery(id+"F1.opExtrude","SWEPT_EDGE",EDGE,{"disambiguationData":[OSD([sQuery(id+"F0.wireOp",EDGE,"E5.top"),sQuery(id+"F0.wireOp",EDGE,"E5.right")])]});
            var Q3;
            Q3=makeQuery(id+"F1.opExtrude","SWEPT_EDGE",EDGE,{"disambiguationData":[OSD([sQuery(id+"F0.wireOp",EDGE,"E5.top"),sQuery(id+"F0.wireOp",EDGE,"E5.left")])]});
            fillet(context, id + "F2", {"entities" : qUnion([Q0, Q1, Q2, Q3]), "radius" : 4 * mm, "tangentPropagation" : true, "allowEdgeOverflow" : false});
        }
        {
            var Q0;
            Q0=makeQuery(id+"F0.imprint","IMPRINT",FACE,{"disambiguationData":[TD([[makeQuery(id+"F0.imprint","IMPRINT",EDGE,{"derivedFrom":sQuery(id+"F0.wireOp",EDGE,"E1")}),-1.0]])]});
            var Q1;
            Q1=makeQuery(id+"F0.imprint","IMPRINT",FACE,{"disambiguationData":[TD([[makeQuery(id+"F0.imprint","IMPRINT",EDGE,{"derivedFrom":sQuery(id+"F0.wireOp",EDGE,"E2")}),-1.0]])]});
            var Q2;
            Q2=makeQuery(id+"F0.imprint","IMPRINT",FACE,{"disambiguationData":[TD([[makeQuery(id+"F0.imprint","IMPRINT",EDGE,{"derivedFrom":sQuery(id+"F0.wireOp",EDGE,"E3")}),-1.0]])]});
            var Q3;
            Q3=makeQuery(id+"F0.imprint","IMPRINT",FACE,{"disambiguationData":[TD([[makeQuery(id+"F0.imprint","IMPRINT",EDGE,{"derivedFrom":sQuery(id+"F0.wireOp",EDGE,"E4")}),-1.0]])]});
            var Q4;
            {var subQ2=sQuery(id+"F0.wireOp",EDGE,"E0.bottom");var subQ4=sQuery(id+"F0.wireOp",EDGE,"E1");var subQ5=makeQuery(id+"F0.imprint","INTERSECT",VERTEX,{"derivedFrom":[subQ2,subQ4]});Q4=makeQuery(id+"F0.imprint","IMPRINT",FACE,{"disambiguationData":[TD([[makeQuery(id+"F0.imprint","IMPRINT",EDGE,{"disambiguationData":[TD([[subQ5,-1.0]])],"derivedFrom":subQ2}),1.0]])]});}
            var Q5;
            {var subQ3=sQuery(id+"F0.wireOp",EDGE,"E0.top");var subQ5=sQuery(id+"F0.wireOp",EDGE,"E169.MirrorC");var subQ8=makeQuery(id+"F0.imprint","INTERSECT",VERTEX,{"derivedFrom":[subQ3,subQ5]});Q5=makeQuery(id+"F0.imprint","IMPRINT",FACE,{"disambiguationData":[TD([[makeQuery(id+"F0.imprint","IMPRINT",EDGE,{"disambiguationData":[TD([[subQ8,-1.0]])],"derivedFrom":subQ3}),-1.0]])]});}
            var Q6;
            {var subQ0=sQuery(id+"F0.wireOp",EDGE,"E167.MirrorC");var subQ3=sQuery(id+"F0.wireOp",EDGE,"E0.right");var subQ4=makeQuery(id+"F0.imprint","INTERSECT",VERTEX,{"derivedFrom":[subQ3,subQ0]});Q6=makeQuery(id+"F0.imprint","IMPRINT",FACE,{"disambiguationData":[TD([[makeQuery(id+"F0.imprint","IMPRINT",EDGE,{"disambiguationData":[TD([[subQ4,-1.0]])],"derivedFrom":subQ3}),1.0]])]});}
            var Q7;
            {var subQ1=sQuery(id+"F0.wireOp",EDGE,"E0.top");var subQ5=sQuery(id+"F0.wireOp",EDGE,"E168.MirrorC");var subQ8=makeQuery(id+"F0.imprint","INTERSECT",VERTEX,{"derivedFrom":[subQ1,subQ5]});Q7=makeQuery(id+"F0.imprint","IMPRINT",FACE,{"disambiguationData":[TD([[makeQuery(id+"F0.imprint","IMPRINT",EDGE,{"disambiguationData":[TD([[subQ8,-1.0]])],"derivedFrom":subQ1}),-1.0]])]});}
            var Q8;
            {var subQ0=sQuery(id+"F0.wireOp",EDGE,"E167.MirrorC");var subQ2=sQuery(id+"F0.wireOp",EDGE,"E0.bottom");var subQ3=makeQuery(id+"F0.imprint","INTERSECT",VERTEX,{"derivedFrom":[subQ2,subQ0]});Q8=makeQuery(id+"F0.imprint","IMPRINT",FACE,{"disambiguationData":[TD([[makeQuery(id+"F0.imprint","IMPRINT",EDGE,{"disambiguationData":[TD([[subQ3,-1.0]])],"derivedFrom":subQ2}),1.0]])]});}
            var Q9;
            {var subQ0=sQuery(id+"F0.wireOp",EDGE,"E166");var subQ5=sQuery(id+"F0.wireOp",EDGE,"E0.bottom");var subQ8=makeQuery(id+"F0.imprint","INTERSECT",VERTEX,{"derivedFrom":[subQ5,subQ0]});Q9=makeQuery(id+"F0.imprint","IMPRINT",FACE,{"disambiguationData":[TD([[makeQuery(id+"F0.imprint","IMPRINT",EDGE,{"disambiguationData":[TD([[subQ8,-1.0]])],"derivedFrom":subQ5}),1.0]])]});}
            var Q10;
            {var subQ0=sQuery(id+"F0.wireOp",EDGE,"E0.left");var subQ4=sQuery(id+"F0.wireOp",EDGE,"E166");var subQ7=makeQuery(id+"F0.imprint","INTERSECT",VERTEX,{"derivedFrom":[subQ0,subQ4]});Q10=makeQuery(id+"F0.imprint","IMPRINT",FACE,{"disambiguationData":[TD([[makeQuery(id+"F0.imprint","IMPRINT",EDGE,{"disambiguationData":[TD([[subQ7,-1.0]])],"derivedFrom":subQ0}),-1.0]])]});}
            var Q11;
            {var subQ2=sQuery(id+"F0.wireOp",EDGE,"E0.top");var subQ4=sQuery(id+"F0.wireOp",EDGE,"E4");var subQ5=makeQuery(id+"F0.imprint","INTERSECT",VERTEX,{"derivedFrom":[subQ2,subQ4]});Q11=makeQuery(id+"F0.imprint","IMPRINT",FACE,{"disambiguationData":[TD([[makeQuery(id+"F0.imprint","IMPRINT",EDGE,{"disambiguationData":[TD([[subQ5,-1.0]])],"derivedFrom":subQ2}),-1.0]])]});}
            extrude(context, id + "F3", {"entities" : qUnion([Q0, Q1, Q2, Q3, Q4, Q5, Q6, Q7, Q8, Q9, Q10, Q11]), "operationType" : NewBodyOperationType.ADD, "depth" : 12 * mm, "offsetDistance" : 25 * mm});
        }
        {
            var Q0;
            Q0=makeQuery(id+"F1.opExtrude","CAP_EDGE",EDGE,{"disambiguationData":[OSD([sQuery(id+"F0.wireOp",EDGE,"E5.right")])],"isStart":true});
            fillet(context, id + "F4", {"entities" : qUnion([Q0]), "radius" : 4 * mm, "tangentPropagation" : true, "allowEdgeOverflow" : false});
        }
        {
            var Q0;
            Q0=makeQuery(id+"F1.opExtrude","CAP_FACE",FACE,{"disambiguationData":[OSD([sQuery(id+"F0.wireOp",EDGE,"E1"),sQuery(id+"F0.wireOp",EDGE,"E2"),sQuery(id+"F0.wireOp",EDGE,"E3"),sQuery(id+"F0.wireOp",EDGE,"E4"),sQuery(id+"F0.wireOp",EDGE,"E5.bottom"),sQuery(id+"F0.wireOp",EDGE,"E5.top"),sQuery(id+"F0.wireOp",EDGE,"E5.left"),sQuery(id+"F0.wireOp",EDGE,"E5.right"),sQuery(id+"F0.wireOp",EDGE,"E6"),sQuery(id+"F0.wireOp",EDGE,"E7.0"),sQuery(id+"F0.wireOp",EDGE,"E7.1"),sQuery(id+"F0.wireOp",EDGE,"E7.2"),sQuery(id+"F0.wireOp",EDGE,"E7.3"),sQuery(id+"F0.wireOp",EDGE,"E7.4"),sQuery(id+"F0.wireOp",EDGE,"E7.5"),sQuery(id+"F0.wireOp",EDGE,"E8.0.1.1"),sQuery(id+"F0.wireOp",EDGE,"E8.0.1.4"),sQuery(id+"F0.wireOp",EDGE,"E8.0.1.5"),sQuery(id+"F0.wireOp",EDGE,"E8.0.1.6"),sQuery(id+"F0.wireOp",EDGE,"E8.0.1.7"),sQuery(id+"F0.wireOp",EDGE,"E8.0.1.8"),sQuery(id+"F0.wireOp",EDGE,"E8.1.0.1"),sQuery(id+"F0.wireOp",EDGE,"E8.1.0.4"),sQuery(id+"F0.wireOp",EDGE,"E8.1.0.5"),sQuery(id+"F0.wireOp",EDGE,"E8.1.0.6"),sQuery(id+"F0.wireOp",EDGE,"E8.1.0.7"),sQuery(id+"F0.wireOp",EDGE,"E8.1.0.8"),sQuery(id+"F0.wireOp",EDGE,"E8.1.1.1"),sQuery(id+"F0.wireOp",EDGE,"E8.1.1.4"),sQuery(id+"F0.wireOp",EDGE,"E8.1.1.5"),sQuery(id+"F0.wireOp",EDGE,"E8.1.1.6"),sQuery(id+"F0.wireOp",EDGE,"E8.1.1.7"),sQuery(id+"F0.wireOp",EDGE,"E8.1.1.8"),sQuery(id+"F0.wireOp",EDGE,"E8.2.0.1"),sQuery(id+"F0.wireOp",EDGE,"E8.2.0.4"),sQuery(id+"F0.wireOp",EDGE,"E8.2.0.5"),sQuery(id+"F0.wireOp",EDGE,"E8.2.0.6"),sQuery(id+"F0.wireOp",EDGE,"E8.2.0.7"),sQuery(id+"F0.wireOp",EDGE,"E8.2.0.8"),sQuery(id+"F0.wireOp",EDGE,"E8.2.1.1"),sQuery(id+"F0.wireOp",EDGE,"E8.2.1.4"),sQuery(id+"F0.wireOp",EDGE,"E8.2.1.5"),sQuery(id+"F0.wireOp",EDGE,"E8.2.1.6"),sQuery(id+"F0.wireOp",EDGE,"E8.2.1.7"),sQuery(id+"F0.wireOp",EDGE,"E8.2.1.8"),sQuery(id+"F0.wireOp",EDGE,"E8.3.0.5"),sQuery(id+"F0.wireOp",EDGE,"E8.3.0.6"),sQuery(id+"F0.wireOp",EDGE,"E8.3.0.7"),sQuery(id+"F0.wireOp",EDGE,"E8.3.1.6"),sQuery(id+"F0.wireOp",EDGE,"E9.0"),sQuery(id+"F0.wireOp",EDGE,"E9.1"),sQuery(id+"F0.wireOp",EDGE,"E9.2"),sQuery(id+"F0.wireOp",EDGE,"E9.3"),sQuery(id+"F0.wireOp",EDGE,"E9.4"),sQuery(id+"F0.wireOp",EDGE,"E9.5"),sQuery(id+"F0.wireOp",EDGE,"E13.0.1.0"),sQuery(id+"F0.wireOp",EDGE,"E13.0.1.1"),sQuery(id+"F0.wireOp",EDGE,"E13.0.1.2"),sQuery(id+"F0.wireOp",EDGE,"E13.0.1.4"),sQuery(id+"F0.wireOp",EDGE,"E13.0.1.6"),sQuery(id+"F0.wireOp",EDGE,"E13.1.0.0"),sQuery(id+"F0.wireOp",EDGE,"E13.1.0.1"),sQuery(id+"F0.wireOp",EDGE,"E13.1.0.2"),sQuery(id+"F0.wireOp",EDGE,"E13.1.0.4"),sQuery(id+"F0.wireOp",EDGE,"E13.1.0.5"),sQuery(id+"F0.wireOp",EDGE,"E13.1.0.6"),sQuery(id+"F0.wireOp",EDGE,"E13.1.1.0"),sQuery(id+"F0.wireOp",EDGE,"E13.1.1.1"),sQuery(id+"F0.wireOp",EDGE,"E13.1.1.2"),sQuery(id+"F0.wireOp",EDGE,"E13.2.0.0"),sQuery(id+"F0.wireOp",EDGE,"E13.2.0.1"),sQuery(id+"F0.wireOp",EDGE,"E13.2.0.2"),sQuery(id+"F0.wireOp",EDGE,"E13.2.0.4"),sQuery(id+"F0.wireOp",EDGE,"E13.2.0.5"),sQuery(id+"F0.wireOp",EDGE,"E13.2.0.6"),sQuery(id+"F0.wireOp",EDGE,"E14.trimOffspring"),sQuery(id+"F0.wireOp",EDGE,"E15.trimOffspring"),sQuery(id+"F0.wireOp",EDGE,"E16.MirrorCS"),sQuery(id+"F0.wireOp",EDGE,"E17.MirrorCS"),sQuery(id+"F0.wireOp",EDGE,"E18.MirrorCS"),sQuery(id+"F0.wireOp",EDGE,"E19.MirrorCS"),sQuery(id+"F0.wireOp",EDGE,"E20.MirrorCS"),sQuery(id+"F0.wireOp",EDGE,"E21.MirrorCS"),sQuery(id+"F0.wireOp",EDGE,"E22.MirrorCS"),sQuery(id+"F0.wireOp",EDGE,"E23.MirrorCS"),sQuery(id+"F0.wireOp",EDGE,"E24.MirrorCS"),sQuery(id+"F0.wireOp",EDGE,"E25.MirrorCS"),sQuery(id+"F0.wireOp",EDGE,"E26.MirrorCS"),sQuery(id+"F0.wireOp",EDGE,"E27.MirrorCS"),sQuery(id+"F0.wireOp",EDGE,"E28.MirrorCS"),sQuery(id+"F0.wireOp",EDGE,"E29.MirrorCS"),sQuery(id+"F0.wireOp",EDGE,"E30.MirrorCS"),sQuery(id+"F0.wireOp",EDGE,"E31.MirrorCS"),sQuery(id+"F0.wireOp",EDGE,"E32.MirrorCS"),sQuery(id+"F0.wireOp",EDGE,"E33.MirrorCS"),sQuery(id+"F0.wireOp",EDGE,"E34.MirrorCS"),sQuery(id+"F0.wireOp",EDGE,"E35.MirrorCS"),sQuery(id+"F0.wireOp",EDGE,"E36.MirrorCS"),sQuery(id+"F0.wireOp",EDGE,"E38.MirrorCS"),sQuery(id+"F0.wireOp",EDGE,"E49.MirrorCS"),sQuery(id+"F0.wireOp",EDGE,"E51.MirrorCS"),sQuery(id+"F0.wireOp",EDGE,"E52.MirrorCS"),sQuery(id+"F0.wireOp",EDGE,"E53.MirrorCS"),sQuery(id+"F0.wireOp",EDGE,"E54.MirrorCS"),sQuery(id+"F0.wireOp",EDGE,"E55.MirrorCS"),sQuery(id+"F0.wireOp",EDGE,"E56.MirrorCS"),sQuery(id+"F0.wireOp",EDGE,"E57.MirrorCS"),sQuery(id+"F0.wireOp",EDGE,"E58.MirrorCS"),sQuery(id+"F0.wireOp",EDGE,"E59.MirrorCS"),sQuery(id+"F0.wireOp",EDGE,"E60.MirrorCS"),sQuery(id+"F0.wireOp",EDGE,"E61.MirrorCS"),sQuery(id+"F0.wireOp",EDGE,"E62.MirrorCS"),sQuery(id+"F0.wireOp",EDGE,"E63.MirrorCS"),sQuery(id+"F0.wireOp",EDGE,"E64.MirrorCS"),sQuery(id+"F0.wireOp",EDGE,"E65.MirrorCS"),sQuery(id+"F0.wireOp",EDGE,"E66.MirrorCS"),sQuery(id+"F0.wireOp",EDGE,"E67.MirrorCS"),sQuery(id+"F0.wireOp",EDGE,"E68.MirrorCS"),sQuery(id+"F0.wireOp",EDGE,"E69.MirrorCS"),sQuery(id+"F0.wireOp",EDGE,"E70.MirrorCS"),sQuery(id+"F0.wireOp",EDGE,"E71.MirrorCS"),sQuery(id+"F0.wireOp",EDGE,"E72.MirrorCS"),sQuery(id+"F0.wireOp",EDGE,"E73.MirrorCS"),sQuery(id+"F0.wireOp",EDGE,"E74.MirrorCS"),sQuery(id+"F0.wireOp",EDGE,"E75.MirrorCS"),sQuery(id+"F0.wireOp",EDGE,"E76.MirrorCS"),sQuery(id+"F0.wireOp",EDGE,"E77.MirrorCS"),sQuery(id+"F0.wireOp",EDGE,"E78.MirrorCS"),sQuery(id+"F0.wireOp",EDGE,"E79.MirrorCS"),sQuery(id+"F0.wireOp",EDGE,"E80.MirrorCS"),sQuery(id+"F0.wireOp",EDGE,"E81.MirrorCS"),sQuery(id+"F0.wireOp",EDGE,"E82.MirrorCS"),sQuery(id+"F0.wireOp",EDGE,"E83.MirrorCS"),sQuery(id+"F0.wireOp",EDGE,"E84.MirrorCS"),sQuery(id+"F0.wireOp",EDGE,"E85.MirrorCS"),sQuery(id+"F0.wireOp",EDGE,"E86.MirrorCS"),sQuery(id+"F0.wireOp",EDGE,"E87.MirrorCS"),sQuery(id+"F0.wireOp",EDGE,"E88.MirrorCS"),sQuery(id+"F0.wireOp",EDGE,"E89.MirrorCS"),sQuery(id+"F0.wireOp",EDGE,"E90.MirrorCS"),sQuery(id+"F0.wireOp",EDGE,"E91.MirrorCS"),sQuery(id+"F0.wireOp",EDGE,"E92.MirrorCS"),sQuery(id+"F0.wireOp",EDGE,"E93.MirrorCS"),sQuery(id+"F0.wireOp",EDGE,"E94.MirrorCS"),sQuery(id+"F0.wireOp",EDGE,"E95.MirrorCS"),sQuery(id+"F0.wireOp",EDGE,"E96.MirrorCS"),sQuery(id+"F0.wireOp",EDGE,"E97.MirrorCS"),sQuery(id+"F0.wireOp",EDGE,"E98.MirrorCS"),sQuery(id+"F0.wireOp",EDGE,"E99.MirrorCS"),sQuery(id+"F0.wireOp",EDGE,"E100.MirrorCS"),sQuery(id+"F0.wireOp",EDGE,"E101.MirrorCS"),sQuery(id+"F0.wireOp",EDGE,"E103.MirrorCS"),sQuery(id+"F0.wireOp",EDGE,"E104.MirrorCS"),sQuery(id+"F0.wireOp",EDGE,"E105.MirrorCS"),sQuery(id+"F0.wireOp",EDGE,"E102.MirrorCS"),sQuery(id+"F0.wireOp",EDGE,"E106.MirrorCS"),sQuery(id+"F0.wireOp",EDGE,"E107.MirrorCS"),sQuery(id+"F0.wireOp",EDGE,"E108.MirrorCS"),sQuery(id+"F0.wireOp",EDGE,"E109.MirrorCS"),sQuery(id+"F0.wireOp",EDGE,"E110.MirrorCS"),sQuery(id+"F0.wireOp",EDGE,"E111.MirrorCS"),sQuery(id+"F0.wireOp",EDGE,"E112.MirrorCS"),sQuery(id+"F0.wireOp",EDGE,"E113.MirrorCS"),sQuery(id+"F0.wireOp",EDGE,"E114.MirrorCS"),sQuery(id+"F0.wireOp",EDGE,"E115.MirrorCS"),sQuery(id+"F0.wireOp",EDGE,"E116.MirrorCS"),sQuery(id+"F0.wireOp",EDGE,"E117.MirrorCS"),sQuery(id+"F0.wireOp",EDGE,"E118.MirrorCS"),sQuery(id+"F0.wireOp",EDGE,"E119.MirrorCS"),sQuery(id+"F0.wireOp",EDGE,"E120.MirrorCS"),sQuery(id+"F0.wireOp",EDGE,"E121.MirrorCS"),sQuery(id+"F0.wireOp",EDGE,"E122.MirrorCS"),sQuery(id+"F0.wireOp",EDGE,"E123.MirrorCS"),sQuery(id+"F0.wireOp",EDGE,"E124.MirrorCS"),sQuery(id+"F0.wireOp",EDGE,"E125.MirrorCS"),sQuery(id+"F0.wireOp",EDGE,"E126.MirrorCS"),sQuery(id+"F0.wireOp",EDGE,"E127.MirrorCS"),sQuery(id+"F0.wireOp",EDGE,"E128.MirrorCS"),sQuery(id+"F0.wireOp",EDGE,"E129.MirrorCS"),sQuery(id+"F0.wireOp",EDGE,"E130.MirrorCS"),sQuery(id+"F0.wireOp",EDGE,"E131.MirrorCS"),sQuery(id+"F0.wireOp",EDGE,"E132.MirrorCS"),sQuery(id+"F0.wireOp",EDGE,"E133.MirrorCS"),sQuery(id+"F0.wireOp",EDGE,"E134.MirrorCS"),sQuery(id+"F0.wireOp",EDGE,"E135.MirrorCS"),sQuery(id+"F0.wireOp",EDGE,"E136.MirrorCS"),sQuery(id+"F0.wireOp",EDGE,"E137.MirrorCS"),sQuery(id+"F0.wireOp",EDGE,"E138.MirrorCS"),sQuery(id+"F0.wireOp",EDGE,"E139.MirrorCS"),sQuery(id+"F0.wireOp",EDGE,"E140.MirrorCS"),sQuery(id+"F0.wireOp",EDGE,"E141.MirrorCS"),sQuery(id+"F0.wireOp",EDGE,"E142.MirrorCS"),sQuery(id+"F0.wireOp",EDGE,"E143.MirrorCS"),sQuery(id+"F0.wireOp",EDGE,"E144.MirrorCS"),sQuery(id+"F0.wireOp",EDGE,"E145.MirrorCS"),sQuery(id+"F0.wireOp",EDGE,"E146.MirrorCS"),sQuery(id+"F0.wireOp",EDGE,"E147.MirrorCS"),sQuery(id+"F0.wireOp",EDGE,"E148.MirrorCS"),sQuery(id+"F0.wireOp",EDGE,"E149.MirrorCS"),sQuery(id+"F0.wireOp",EDGE,"E150.MirrorCS"),sQuery(id+"F0.wireOp",EDGE,"E151.MirrorCS"),sQuery(id+"F0.wireOp",EDGE,"E152.MirrorCS"),sQuery(id+"F0.wireOp",EDGE,"E153.MirrorCS"),sQuery(id+"F0.wireOp",EDGE,"E154.MirrorCS"),sQuery(id+"F0.wireOp",EDGE,"E155.MirrorCS"),sQuery(id+"F0.wireOp",EDGE,"E156.MirrorCS"),sQuery(id+"F0.wireOp",EDGE,"E157.MirrorCS"),sQuery(id+"F0.wireOp",EDGE,"E158.MirrorCS"),sQuery(id+"F0.wireOp",EDGE,"E159.MirrorCS"),sQuery(id+"F0.wireOp",EDGE,"E160.MirrorCS"),sQuery(id+"F0.wireOp",EDGE,"E161.MirrorCS"),sQuery(id+"F0.wireOp",EDGE,"E162.MirrorCS"),sQuery(id+"F0.wireOp",EDGE,"E163.MirrorCS"),sQuery(id+"F0.wireOp",EDGE,"E164.MirrorCS"),sQuery(id+"F0.wireOp",EDGE,"E165.MirrorCS")])],"isStart":true});
            var sketch = newSketch(context, id + "F5", { "sketchPlane" : qUnion([Q0])});
            skCircle(sketch, "E170", {"center": v(-36, 36) * mm, "radius": 4 * mm});
            skCircle(sketch, "E171.MirrorC", {"center": v(36, 36) * mm, "radius": 4 * mm});
            skCircle(sketch, "E172.MirrorC", {"center": v(36, -36) * mm, "radius": 4 * mm});
            skCircle(sketch, "E173.MirrorC", {"center": v(-36, -36) * mm, "radius": 4 * mm});
            skSolve(sketch);
        }
        {
            var Q0;
            {var subQ3=sQuery(id+"F0.wireOp",EDGE,"E4");var subQ9=makeQuery(id+"F1.opExtrude","CAP_EDGE",EDGE,{"disambiguationData":[OSD([subQ3])],"isStart":true});Q0=makeQuery(id+"F5.imprint","IMPRINT",FACE,{"disambiguationData":[TD([[makeQuery(id+"F5.imprint","IMPRINT",EDGE,{"derivedFrom":subQ9}),-1.0]])]});}
            var Q1;
            {var subQ3=sQuery(id+"F0.wireOp",EDGE,"E4");var subQ9=makeQuery(id+"F1.opExtrude","CAP_EDGE",EDGE,{"disambiguationData":[OSD([subQ3])],"isStart":true});Q1=makeQuery(id+"F5.imprint","IMPRINT",FACE,{"disambiguationData":[TD([[makeQuery(id+"F5.imprint","IMPRINT",EDGE,{"derivedFrom":subQ9}),1.0]])]});}
            var Q2;
            {var subQ3=sQuery(id+"F0.wireOp",EDGE,"E3");var subQ9=makeQuery(id+"F1.opExtrude","CAP_EDGE",EDGE,{"disambiguationData":[OSD([subQ3])],"isStart":true});Q2=makeQuery(id+"F5.imprint","IMPRINT",FACE,{"disambiguationData":[TD([[makeQuery(id+"F5.imprint","IMPRINT",EDGE,{"derivedFrom":subQ9}),-1.0]])]});}
            var Q3;
            {var subQ3=sQuery(id+"F0.wireOp",EDGE,"E3");var subQ9=makeQuery(id+"F1.opExtrude","CAP_EDGE",EDGE,{"disambiguationData":[OSD([subQ3])],"isStart":true});Q3=makeQuery(id+"F5.imprint","IMPRINT",FACE,{"disambiguationData":[TD([[makeQuery(id+"F5.imprint","IMPRINT",EDGE,{"derivedFrom":subQ9}),1.0]])]});}
            var Q4;
            {var subQ3=sQuery(id+"F0.wireOp",EDGE,"E1");var subQ9=makeQuery(id+"F1.opExtrude","CAP_EDGE",EDGE,{"disambiguationData":[OSD([subQ3])],"isStart":true});Q4=makeQuery(id+"F5.imprint","IMPRINT",FACE,{"disambiguationData":[TD([[makeQuery(id+"F5.imprint","IMPRINT",EDGE,{"derivedFrom":subQ9}),1.0]])]});}
            var Q5;
            {var subQ3=sQuery(id+"F0.wireOp",EDGE,"E1");var subQ9=makeQuery(id+"F1.opExtrude","CAP_EDGE",EDGE,{"disambiguationData":[OSD([subQ3])],"isStart":true});Q5=makeQuery(id+"F5.imprint","IMPRINT",FACE,{"disambiguationData":[TD([[makeQuery(id+"F5.imprint","IMPRINT",EDGE,{"derivedFrom":subQ9}),-1.0]])]});}
            var Q6;
            {var subQ3=sQuery(id+"F0.wireOp",EDGE,"E2");var subQ9=makeQuery(id+"F1.opExtrude","CAP_EDGE",EDGE,{"disambiguationData":[OSD([subQ3])],"isStart":true});Q6=makeQuery(id+"F5.imprint","IMPRINT",FACE,{"disambiguationData":[TD([[makeQuery(id+"F5.imprint","IMPRINT",EDGE,{"derivedFrom":subQ9}),-1.0]])]});}
            var Q7;
            {var subQ3=sQuery(id+"F0.wireOp",EDGE,"E2");var subQ9=makeQuery(id+"F1.opExtrude","CAP_EDGE",EDGE,{"disambiguationData":[OSD([subQ3])],"isStart":true});Q7=makeQuery(id+"F5.imprint","IMPRINT",FACE,{"disambiguationData":[TD([[makeQuery(id+"F5.imprint","IMPRINT",EDGE,{"derivedFrom":subQ9}),1.0]])]});}
            extrude(context, id + "F6", {"entities" : qUnion([Q0, Q1, Q2, Q3, Q4, Q5, Q6, Q7]), "operationType" : NewBodyOperationType.REMOVE, "oppositeDirection" : true, "depth" : 4 * mm, "offsetDistance" : 25 * mm});
        }
    });
